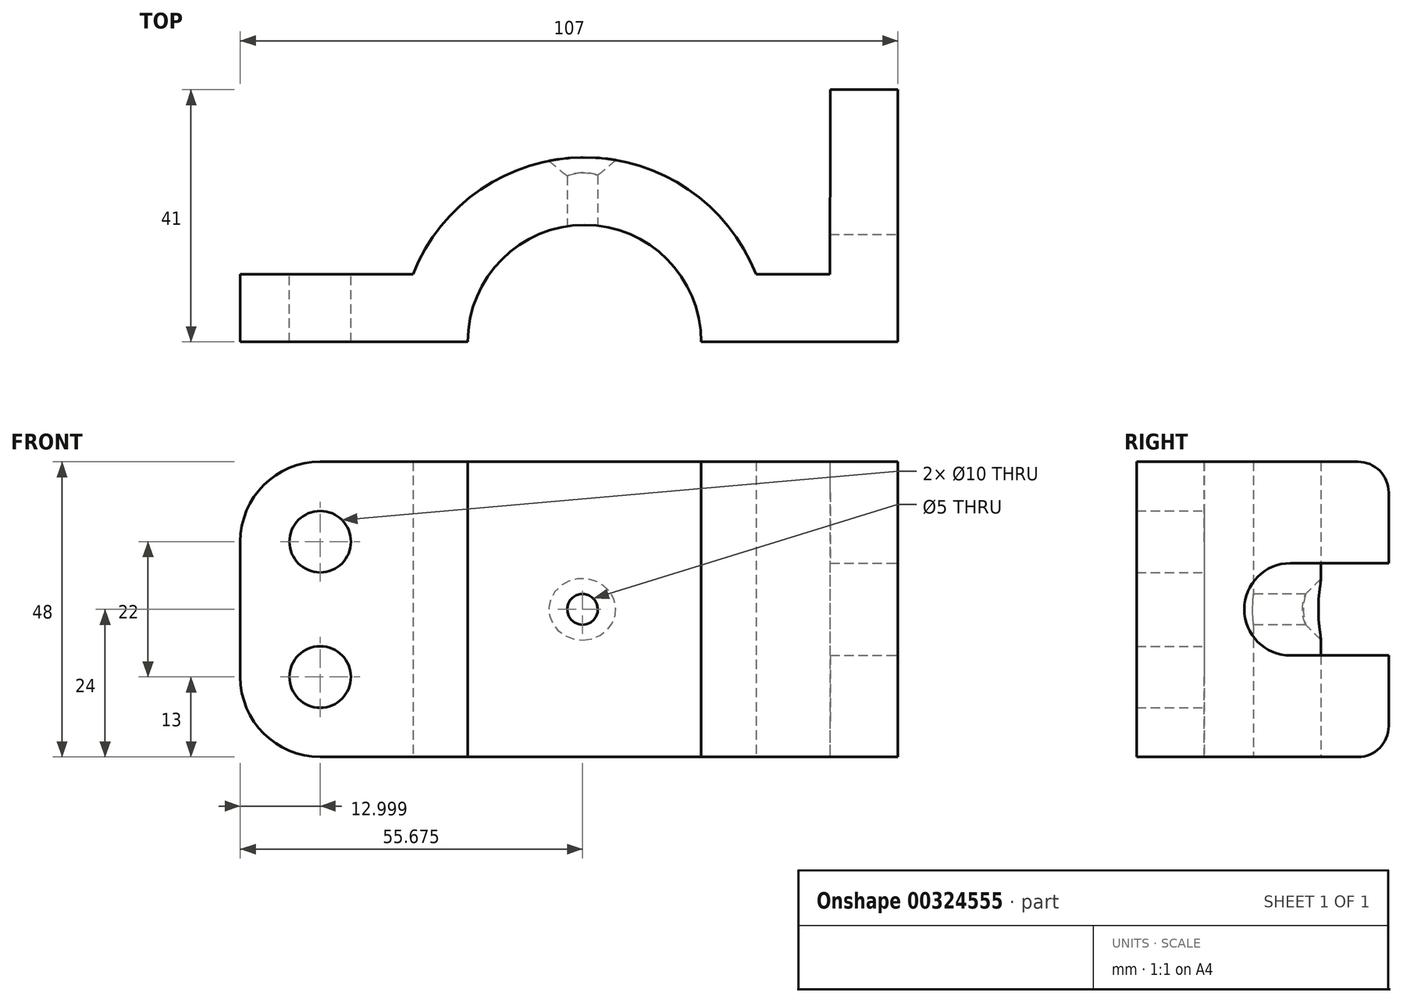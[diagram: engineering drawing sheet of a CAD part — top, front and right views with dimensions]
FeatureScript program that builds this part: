
annotation { "Feature Type Name" : "Feature", "Feature Type Description" : "" }
export const myFeature = defineFeature(function(context is Context, id is Id, definition is map)
    precondition{}
    {
        {
            var Q0;
            Q0=qCreatedBy(makeId("Top.planeOp"),FACE);
            var sketch = newSketch(context, id + "F0", { "sketchPlane" : qUnion([Q0])});
            skLineSegment(sketch, "E0", {"start": v(-83.91, -30.32) * mm, "end": v(-46.91, -30.32) * mm});
            skArc(sketch, "E1", {"start": v(-8.91, -30.32) * mm, "mid": v(-27.91, -11.32) * mm, "end": v(-46.91, -30.32) * mm});
            skLineSegment(sketch, "E2", {"start": v(-8.91, -30.32) * mm, "end": v(23.09, -30.32) * mm});
            skLineSegment(sketch, "E3", {"start": v(-83.91, -30.32) * mm, "end": v(-83.91, -19.32) * mm});
            skLineSegment(sketch, "E4", {"start": v(0, -19.32) * mm, "end": v(12, -19.32) * mm});
            skLineSegment(sketch, "E5", {"start": v(23.09, -30.32) * mm, "end": v(23.09, 10.68) * mm});
            skLineSegment(sketch, "E6", {"start": v(23.09, 10.68) * mm, "end": v(12.09, 10.68) * mm});
            skLineSegment(sketch, "E7", {"start": v(12.09, 10.68) * mm, "end": v(12, -19.32) * mm});
            skLineSegment(sketch, "E8", {"start": v(-83.91, -19.32) * mm, "end": v(-55.82, -19.32) * mm});
            skArc(sketch, "E9", {"start": v(0, -19.32) * mm, "mid": v(-27.91, -0.32) * mm, "end": v(-55.82, -19.32) * mm});
            skSolve(sketch);
        }
        {
            var Q0;
            Q0=makeQuery(id+"F0.imprint","IMPRINT",FACE,{"disambiguationData":[TD([[makeQuery(id+"F0.imprint","IMPRINT",EDGE,{"derivedFrom":sQuery(id+"F0.wireOp",EDGE,"E0")}),1.0]])]});
            extrude(context, id + "F1", {"entities" : qUnion([Q0]), "depth" : 48 * mm});
        }
        {
            var Q0;
            Q0=makeQuery(id+"F1.opExtrude","SWEPT_FACE",FACE,{"disambiguationData":[OSD([sQuery(id+"F0.wireOp",EDGE,"E8")])]});
            var sketch = newSketch(context, id + "F2", { "sketchPlane" : qUnion([Q0])});
            skPoint(sketch, "E10", {"position": v(70.91, 13) * mm});
            skPoint(sketch, "E11", {"position": v(70.91, 35) * mm});
            skCircle(sketch, "E12", {"center": v(70.91, 13) * mm, "radius": 5 * mm});
            skCircle(sketch, "E13", {"center": v(70.91, 35) * mm, "radius": 5 * mm});
            skPoint(sketch, "E14", {"position": v(28.24, 24) * mm});
            skArc(sketch, "E15", {"start": v(70.91, 0) * mm, "mid": v(80.1, 3.8) * mm, "end": v(83.91, 13) * mm});
            skArc(sketch, "E16", {"start": v(83.91, 35) * mm, "mid": v(80.1, 44.2) * mm, "end": v(70.91, 48) * mm});
            skSolve(sketch);
        }
        {
            var Q0;
            Q0=makeQuery(id+"F1.opExtrude","SWEPT_FACE",FACE,{"disambiguationData":[OSD([sQuery(id+"F0.wireOp",EDGE,"E5")])]});
            var sketch = newSketch(context, id + "F3", { "sketchPlane" : qUnion([Q0])});
            skLineSegment(sketch, "E17", {"start": v(10.68, 24) * mm, "end": v(-30.32, 24) * mm});
            skLineSegment(sketch, "E18", {"start": v(-9.82, 48) * mm, "end": v(-9.82, 0) * mm});
            skPoint(sketch, "E19", {"position": v(10.68, 16.5) * mm});
            skPoint(sketch, "E20", {"position": v(10.68, 31.5) * mm});
            skLineSegment(sketch, "E21", {"start": v(10.68, 31.5) * mm, "end": v(-5.32, 31.5) * mm});
            skLineSegment(sketch, "E22", {"start": v(10.68, 16.5) * mm, "end": v(-5.32, 16.5) * mm});
            skArc(sketch, "E23", {"start": v(-5.32, 31.5) * mm, "mid": v(-12.82, 24) * mm, "end": v(-5.32, 16.5) * mm});
            skLineSegment(sketch, "E24", {"start": v(-5.32, 31.5) * mm, "end": v(-5.32, 16.5) * mm});
            skSolve(sketch);
        }
        {
            var Q0;
            {var subQ5=sQuery(id+"F3.wireOp",EDGE,"E21");Q0=makeQuery(id+"F3.imprint","IMPRINT",FACE,{"disambiguationData":[TD([[makeQuery(id+"F3.imprint","IMPRINT",EDGE,{"derivedFrom":subQ5}),1.0]])]});}
            var Q1;
            {var subQ5=sQuery(id+"F3.wireOp",EDGE,"E22");Q1=makeQuery(id+"F3.imprint","IMPRINT",FACE,{"disambiguationData":[TD([[makeQuery(id+"F3.imprint","IMPRINT",EDGE,{"derivedFrom":subQ5}),-1.0]])]});}
            var Q2;
            {var subQ0=sQuery(id+"F3.wireOp",EDGE,"E24");var subQ1=sQuery(id+"F3.wireOp",EDGE,"E17");var subQ2=makeQuery(id+"F3.imprint","INTERSECT",VERTEX,{"derivedFrom":[subQ1,subQ0]});Q2=makeQuery(id+"F3.imprint","IMPRINT",FACE,{"disambiguationData":[TD([[makeQuery(id+"F3.imprint","IMPRINT",EDGE,{"disambiguationData":[TD([[subQ2,-1.0]])],"derivedFrom":subQ1}),1.0]])]});}
            var Q3;
            {var subQ0=sQuery(id+"F3.wireOp",EDGE,"E24");var subQ1=sQuery(id+"F3.wireOp",EDGE,"E17");var subQ2=makeQuery(id+"F3.imprint","INTERSECT",VERTEX,{"derivedFrom":[subQ1,subQ0]});Q3=makeQuery(id+"F3.imprint","IMPRINT",FACE,{"disambiguationData":[TD([[makeQuery(id+"F3.imprint","IMPRINT",EDGE,{"disambiguationData":[TD([[subQ2,-1.0]])],"derivedFrom":subQ1}),-1.0]])]});}
            var Q4;
            {var subQ0=sQuery(id+"F3.wireOp",EDGE,"E18");var subQ1=sQuery(id+"F3.wireOp",EDGE,"E17");var subQ2=makeQuery(id+"F3.imprint","INTERSECT",VERTEX,{"derivedFrom":[subQ1,subQ0]});Q4=makeQuery(id+"F3.imprint","IMPRINT",FACE,{"disambiguationData":[TD([[makeQuery(id+"F3.imprint","IMPRINT",EDGE,{"disambiguationData":[TD([[subQ2,-1.0]])],"derivedFrom":subQ1}),-1.0]])]});}
            var Q5;
            {var subQ0=sQuery(id+"F3.wireOp",EDGE,"E18");var subQ1=sQuery(id+"F3.wireOp",EDGE,"E17");var subQ2=makeQuery(id+"F3.imprint","INTERSECT",VERTEX,{"derivedFrom":[subQ1,subQ0]});Q5=makeQuery(id+"F3.imprint","IMPRINT",FACE,{"disambiguationData":[TD([[makeQuery(id+"F3.imprint","IMPRINT",EDGE,{"disambiguationData":[TD([[subQ2,-1.0]])],"derivedFrom":subQ1}),1.0]])]});}
            extrude(context, id + "F4", {"entities" : qUnion([Q0, Q1, Q2, Q3, Q4, Q5]), "operationType" : NewBodyOperationType.REMOVE, "oppositeDirection" : true, "depth" : 13 * mm});
        }
        {
            var Q0;
            Q0=makeQuery(id+"F2.imprint","IMPRINT",FACE,{"disambiguationData":[TD([[makeQuery(id+"F2.imprint","IMPRINT",EDGE,{"derivedFrom":sQuery(id+"F2.wireOp",EDGE,"E13")}),1.0]])]});
            var Q1;
            Q1=makeQuery(id+"F2.imprint","IMPRINT",FACE,{"disambiguationData":[TD([[makeQuery(id+"F2.imprint","IMPRINT",EDGE,{"derivedFrom":sQuery(id+"F2.wireOp",EDGE,"E12")}),1.0]])]});
            extrude(context, id + "F5", {"entities" : qUnion([Q0, Q1]), "operationType" : NewBodyOperationType.REMOVE, "oppositeDirection" : true, "depth" : 11 * mm});
        }
        {
            var Q0;
            Q0 = qSketchRegion(id + "F2", true);
            var Q1;
            {var subQ0=sQuery(id+"F2.wireOp",EDGE,"E16");Q1=makeQuery(id+"F2.imprint","IMPRINT",FACE,{"disambiguationData":[TD([[makeQuery(id+"F2.imprint","IMPRINT",EDGE,{"derivedFrom":subQ0}),-1.0]])]});}
            var Q2;
            {var subQ0=sQuery(id+"F2.wireOp",EDGE,"E15");Q2=makeQuery(id+"F2.imprint","IMPRINT",FACE,{"disambiguationData":[TD([[makeQuery(id+"F2.imprint","IMPRINT",EDGE,{"derivedFrom":subQ0}),-1.0]])]});}
            extrude(context, id + "F6", {"entities" : qUnion([Q0, Q1, Q2]), "operationType" : NewBodyOperationType.REMOVE, "endBound" : BoundingType.THROUGH_ALL, "oppositeDirection" : true, "depth" : 11 * mm});
        }
        {
            var Q0;
            Q0=qCreatedBy(makeId("Front.planeOp"),FACE);
            cPlane(context, id + "F7", {"entities" : qUnion([Q0]), "cplaneType" : CPlaneType.OFFSET, "offset" : 40 * mm, "width" : 150 * mm, "height" : 150 * mm});
        }
        {
            var Q0;
            Q0=qCreatedBy(id+"F7.planeOp",FACE);
            var sketch = newSketch(context, id + "F8", { "sketchPlane" : qUnion([Q0])});
            skCircle(sketch, "E25", {"center": v(-28.24, 24) * mm, "radius": 2.5 * mm});
            skSolve(sketch);
        }
        {
            var Q0;
            Q0=makeQuery(id+"F8.imprint","IMPRINT",FACE,{"disambiguationData":[TD([[makeQuery(id+"F8.imprint","IMPRINT",EDGE,{"derivedFrom":sQuery(id+"F8.wireOp",EDGE,"E25")}),1.0]])]});
            extrude(context, id + "F9", {"entities" : qUnion([Q0]), "operationType" : NewBodyOperationType.REMOVE, "endBound" : BoundingType.THROUGH_ALL, "oppositeDirection" : true, "depth" : 25 * mm});
        }
        {
            var Q0;
            Q0=makeQuery(id+"F9.boolean.opBoolean","INTERSECT",EDGE,{"derivedFrom":[makeQuery(id+"F1.opExtrude","SWEPT_FACE",FACE,{"disambiguationData":[OSD([sQuery(id+"F0.wireOp",EDGE,"E9")])]}),makeQuery(id+"F9.opExtrude","SWEPT_FACE",FACE,{"disambiguationData":[OSD([sQuery(id+"F8.wireOp",EDGE,"E25")])]})]});
            chamfer(context, id + "F10", {"entities" : qUnion([Q0]), "chamferType" : ChamferType.OFFSET_ANGLE, "width" : 2.5 * mm, "oppositeDirection" : false, "angle" : 45 * degree, "tangentPropagation" : true});
        }
        {
            var Q0;
            Q0=makeQuery(id+"F1.opExtrude","CAP_EDGE",EDGE,{"disambiguationData":[OSD([sQuery(id+"F0.wireOp",EDGE,"E6")])],"isStart":false});
            var Q1;
            Q1=makeQuery(id+"F1.opExtrude","CAP_EDGE",EDGE,{"disambiguationData":[OSD([sQuery(id+"F0.wireOp",EDGE,"E6")])],"isStart":true});
            fillet(context, id + "F11", {"entities" : qUnion([Q0, Q1]), "radius" : 5 * mm, "tangentPropagation" : true, "allowEdgeOverflow" : false});
        }
    });
